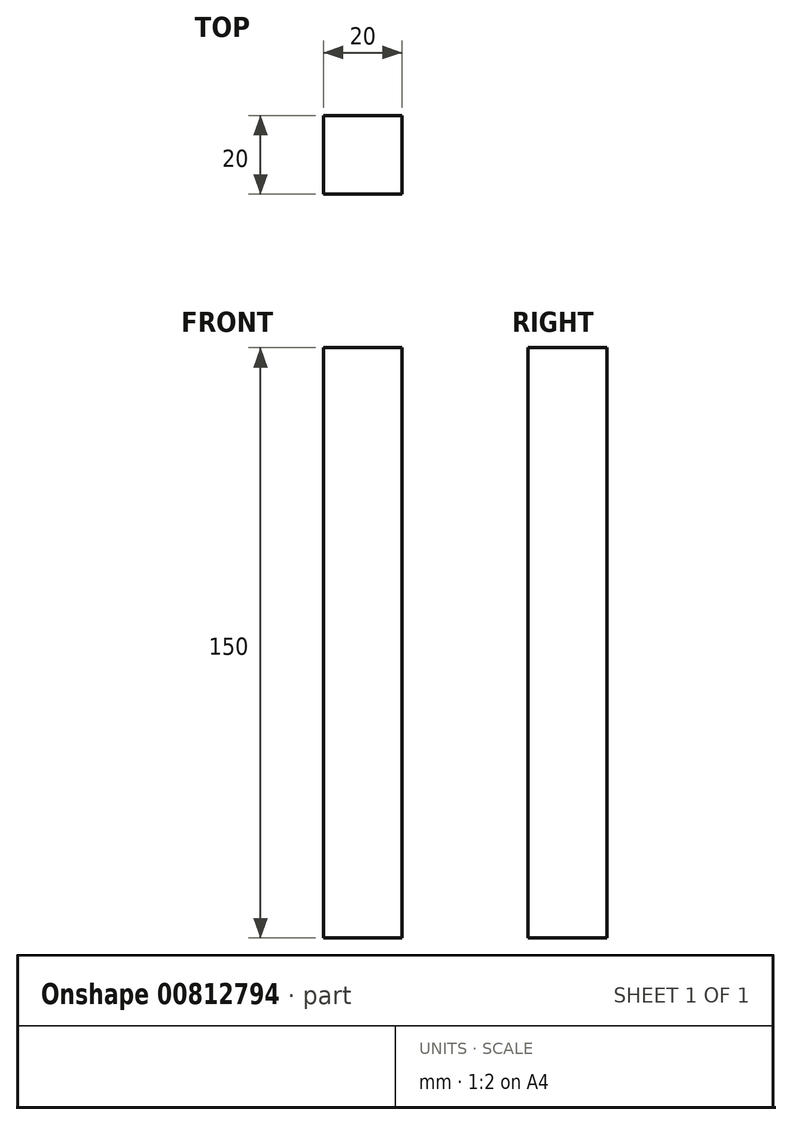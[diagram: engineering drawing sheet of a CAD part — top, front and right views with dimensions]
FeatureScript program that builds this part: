
annotation { "Feature Type Name" : "Feature", "Feature Type Description" : "" }
export const myFeature = defineFeature(function(context is Context, id is Id, definition is map)
    precondition{}
    {
        {
            var Q0;
            Q0=qCreatedBy(makeId("Top.planeOp"),FACE);
            var sketch = newSketch(context, id + "F0", { "sketchPlane" : qUnion([Q0])});
            skLineSegment(sketch, "E0.bottom", {"start": v(-10, -10) * mm, "end": v(10, -10) * mm});
            skLineSegment(sketch, "E0.top", {"start": v(-10, 10) * mm, "end": v(10, 10) * mm});
            skLineSegment(sketch, "E0.left", {"start": v(-10, -10) * mm, "end": v(-10, 10) * mm});
            skLineSegment(sketch, "E0.right", {"start": v(10, -10) * mm, "end": v(10, 10) * mm});
            skSolve(sketch);
        }
        {
            var Q0;
            Q0=makeQuery(id+"F0.imprint","IMPRINT",FACE,{"disambiguationData":[TD([[makeQuery(id+"F0.imprint","IMPRINT",EDGE,{"derivedFrom":sQuery(id+"F0.wireOp",EDGE,"E0.bottom")}),1.0]])]});
            extrude(context, id + "F1", {"entities" : qUnion([Q0]), "depth" : 150 * mm, "offsetDistance" : 25 * mm});
        }
    });
